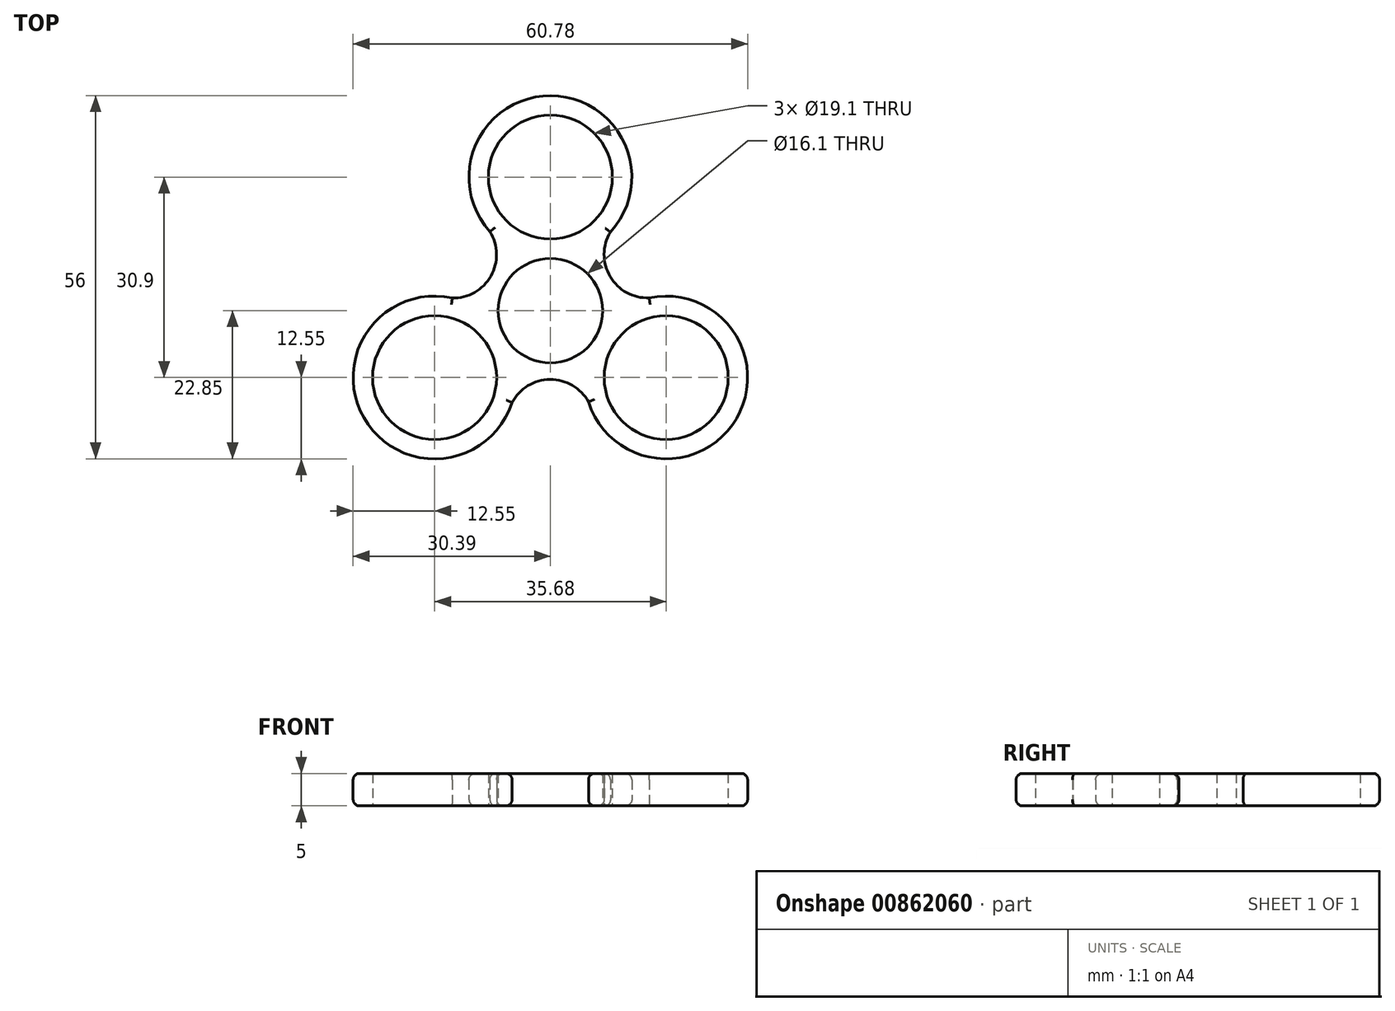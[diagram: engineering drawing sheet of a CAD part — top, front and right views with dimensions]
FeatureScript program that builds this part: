
annotation { "Feature Type Name" : "Feature", "Feature Type Description" : "" }
export const myFeature = defineFeature(function(context is Context, id is Id, definition is map)
    precondition{}
    {
        {
            var Q0;
            Q0=qCreatedBy(makeId("Top.planeOp"),FACE);
            var sketch = newSketch(context, id + "F0", { "sketchPlane" : qUnion([Q0])});
            skCircle(sketch, "E0", {"center": v(0, 0) * mm, "radius": 8.05 * mm});
            skCircle(sketch, "E1", {"center": v(0, 20.6) * mm, "radius": 9.55 * mm});
            skCircle(sketch, "E2.0", {"center": v(0, 20.6) * mm, "radius": 12.55 * mm});
            skPoint(sketch, "E3.center", {"position": v(-0.13, -6.77) * mm});
            skPoint(sketch, "E4.center", {"position": v(-0.64, -0.65) * mm});
            skCircle(sketch, "E5", {"center": v(0, 0) * mm, "radius": 20.6 * mm, "construction": true});
            skPoint(sketch, "E6.center", {"position": v(0, -1) * mm});
            skCircle(sketch, "E7.1.0", {"center": v(-17.84, -10.3) * mm, "radius": 9.55 * mm});
            skCircle(sketch, "E7.1.1", {"center": v(-17.84, -10.3) * mm, "radius": 12.55 * mm});
            skCircle(sketch, "E7.2.0", {"center": v(17.84, -10.3) * mm, "radius": 9.55 * mm});
            skCircle(sketch, "E7.2.1", {"center": v(17.84, -10.3) * mm, "radius": 12.55 * mm});
            skArc(sketch, "E8", {"start": v(9.25, 12.12) * mm, "mid": v(9.2, 5.26) * mm, "end": v(15.22, 1.97) * mm});
            skArc(sketch, "E9.1.0", {"start": v(-15.12, 1.95) * mm, "mid": v(-9.16, 5.34) * mm, "end": v(-9.32, 12.2) * mm});
            skArc(sketch, "E9.2.0", {"start": v(5.87, -14.07) * mm, "mid": v(-0.05, -10.6) * mm, "end": v(-5.9, -14.17) * mm});
            skSolve(sketch);
        }
        {
            var Q0;
            {var subQ5=sQuery(id+"F0.wireOp",EDGE,"E9.1.0");Q0=makeQuery(id+"F0.imprint","IMPRINT",FACE,{"disambiguationData":[TD([[makeQuery(id+"F0.imprint","IMPRINT",EDGE,{"derivedFrom":subQ5}),-1.0]])]});}
            var Q1;
            Q1=makeQuery(id+"F0.imprint","IMPRINT",FACE,{"disambiguationData":[TD([[makeQuery(id+"F0.imprint","IMPRINT",EDGE,{"derivedFrom":sQuery(id+"F0.wireOp",EDGE,"E7.2.0")}),1.0]])]});
            var Q2;
            Q2=makeQuery(id+"F0.imprint","IMPRINT",FACE,{"disambiguationData":[TD([[makeQuery(id+"F0.imprint","IMPRINT",EDGE,{"derivedFrom":sQuery(id+"F0.wireOp",EDGE,"E1")}),1.0]])]});
            var Q3;
            Q3=makeQuery(id+"F0.imprint","IMPRINT",FACE,{"disambiguationData":[TD([[makeQuery(id+"F0.imprint","IMPRINT",EDGE,{"derivedFrom":sQuery(id+"F0.wireOp",EDGE,"E7.1.0")}),1.0]])]});
            var Q4;
            {var subQ5=sQuery(id+"F0.wireOp",EDGE,"E8");Q4=makeQuery(id+"F0.imprint","IMPRINT",FACE,{"disambiguationData":[TD([[makeQuery(id+"F0.imprint","IMPRINT",EDGE,{"derivedFrom":subQ5}),-1.0]])]});}
            var Q5;
            Q5=makeQuery(id+"F0.imprint","IMPRINT",FACE,{"disambiguationData":[TD([[makeQuery(id+"F0.imprint","IMPRINT",EDGE,{"derivedFrom":sQuery(id+"F0.wireOp",EDGE,"E1")}),-1.0]])]});
            var Q6;
            Q6=makeQuery(id+"F0.imprint","IMPRINT",FACE,{"disambiguationData":[TD([[makeQuery(id+"F0.imprint","IMPRINT",EDGE,{"derivedFrom":sQuery(id+"F0.wireOp",EDGE,"E7.1.0")}),-1.0]])]});
            var Q7;
            {var subQ0=sQuery(id+"F0.wireOp",EDGE,"E0");var subQ1=makeQuery(id+"F0.imprint","INTERSECT",VERTEX,{"derivedFrom":[subQ0,sQuery(id+"F0.wireOp",EDGE,"E7.1.1")]});Q7=makeQuery(id+"F0.imprint","IMPRINT",FACE,{"disambiguationData":[TD([[makeQuery(id+"F0.imprint","IMPRINT",EDGE,{"disambiguationData":[TD([[subQ1,1.0]])],"derivedFrom":subQ0}),1.0]])]});}
            var Q8;
            Q8=makeQuery(id+"F0.imprint","IMPRINT",FACE,{"disambiguationData":[TD([[makeQuery(id+"F0.imprint","IMPRINT",EDGE,{"derivedFrom":sQuery(id+"F0.wireOp",EDGE,"E7.2.0")}),-1.0]])]});
            var Q9;
            {var subQ5=sQuery(id+"F0.wireOp",EDGE,"E9.2.0");Q9=makeQuery(id+"F0.imprint","IMPRINT",FACE,{"disambiguationData":[TD([[makeQuery(id+"F0.imprint","IMPRINT",EDGE,{"derivedFrom":subQ5}),-1.0]])]});}
            extrude(context, id + "F1", {"entities" : qUnion([Q0, Q1, Q2, Q3, Q4, Q5, Q6, Q7, Q8, Q9]), "depth" : 5 * mm, "offsetDistance" : 25 * mm});
        }
        {
            var Q0;
            Q0=makeQuery(id+"F0.imprint","IMPRINT",FACE,{"disambiguationData":[TD([[makeQuery(id+"F0.imprint","IMPRINT",EDGE,{"derivedFrom":sQuery(id+"F0.wireOp",EDGE,"E7.1.0")}),1.0]])]});
            var Q1;
            Q1=makeQuery(id+"F0.imprint","IMPRINT",FACE,{"disambiguationData":[TD([[makeQuery(id+"F0.imprint","IMPRINT",EDGE,{"derivedFrom":sQuery(id+"F0.wireOp",EDGE,"E1")}),1.0]])]});
            var Q2;
            Q2=makeQuery(id+"F0.imprint","IMPRINT",FACE,{"disambiguationData":[TD([[makeQuery(id+"F0.imprint","IMPRINT",EDGE,{"derivedFrom":sQuery(id+"F0.wireOp",EDGE,"E7.2.0")}),1.0]])]});
            var Q3;
            {var subQ0=sQuery(id+"F0.wireOp",EDGE,"E0");var subQ1=makeQuery(id+"F0.imprint","INTERSECT",VERTEX,{"derivedFrom":[subQ0,sQuery(id+"F0.wireOp",EDGE,"E7.1.1")]});Q3=makeQuery(id+"F0.imprint","IMPRINT",FACE,{"disambiguationData":[TD([[makeQuery(id+"F0.imprint","IMPRINT",EDGE,{"disambiguationData":[TD([[subQ1,1.0]])],"derivedFrom":subQ0}),1.0]])]});}
            extrude(context, id + "F2", {"entities" : qUnion([Q0, Q1, Q2, Q3]), "operationType" : NewBodyOperationType.REMOVE, "depth" : 25 * mm, "offsetDistance" : 25 * mm});
        }
        {
            var Q0;
            Q0=makeQuery(id+"F1.opExtrude","CAP_EDGE",EDGE,{"disambiguationData":[OSD([sQuery(id+"F0.wireOp",EDGE,"E2.0")])],"isStart":true});
            var Q1;
            Q1=makeQuery(id+"F1.opExtrude","CAP_EDGE",EDGE,{"disambiguationData":[OSD([sQuery(id+"F0.wireOp",EDGE,"E8")])],"isStart":true});
            var Q2;
            Q2=makeQuery(id+"F1.opExtrude","CAP_EDGE",EDGE,{"disambiguationData":[OSD([sQuery(id+"F0.wireOp",EDGE,"E7.2.1")])],"isStart":true});
            var Q3;
            Q3=makeQuery(id+"F1.opExtrude","CAP_EDGE",EDGE,{"disambiguationData":[OSD([sQuery(id+"F0.wireOp",EDGE,"E9.2.0")])],"isStart":true});
            var Q4;
            Q4=makeQuery(id+"F1.opExtrude","CAP_EDGE",EDGE,{"disambiguationData":[OSD([sQuery(id+"F0.wireOp",EDGE,"E7.1.1")])],"isStart":true});
            var Q5;
            Q5=makeQuery(id+"F1.opExtrude","CAP_EDGE",EDGE,{"disambiguationData":[OSD([sQuery(id+"F0.wireOp",EDGE,"E9.1.0")])],"isStart":true});
            var Q6;
            Q6=makeQuery(id+"F1.opExtrude","CAP_EDGE",EDGE,{"disambiguationData":[OSD([sQuery(id+"F0.wireOp",EDGE,"E2.0")])],"isStart":false});
            var Q7;
            Q7=makeQuery(id+"F1.opExtrude","CAP_EDGE",EDGE,{"disambiguationData":[OSD([sQuery(id+"F0.wireOp",EDGE,"E9.1.0")])],"isStart":false});
            var Q8;
            Q8=makeQuery(id+"F1.opExtrude","CAP_EDGE",EDGE,{"disambiguationData":[OSD([sQuery(id+"F0.wireOp",EDGE,"E7.1.1")])],"isStart":false});
            var Q9;
            Q9=makeQuery(id+"F1.opExtrude","CAP_EDGE",EDGE,{"disambiguationData":[OSD([sQuery(id+"F0.wireOp",EDGE,"E9.2.0")])],"isStart":false});
            var Q10;
            Q10=makeQuery(id+"F1.opExtrude","CAP_EDGE",EDGE,{"disambiguationData":[OSD([sQuery(id+"F0.wireOp",EDGE,"E7.2.1")])],"isStart":false});
            var Q11;
            Q11=makeQuery(id+"F1.opExtrude","CAP_EDGE",EDGE,{"disambiguationData":[OSD([sQuery(id+"F0.wireOp",EDGE,"E8")])],"isStart":false});
            fillet(context, id + "F3", {"entities" : qUnion([Q0, Q1, Q2, Q3, Q4, Q5, Q6, Q7, Q8, Q9, Q10, Q11]), "radius" : 1 * mm, "tangentPropagation" : true, "allowEdgeOverflow" : false});
        }
    });
